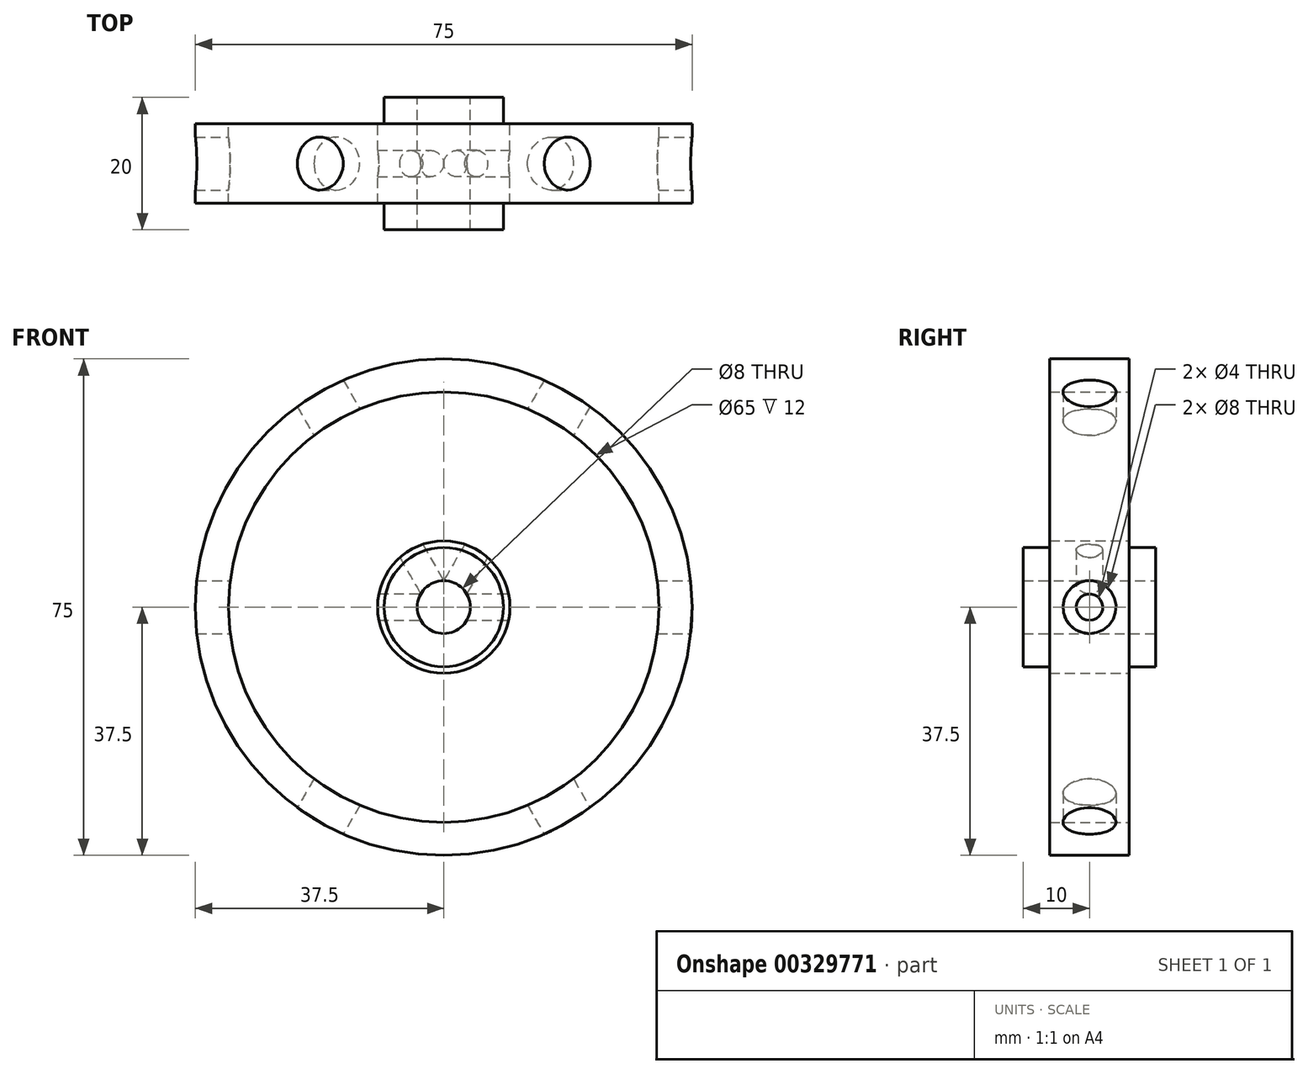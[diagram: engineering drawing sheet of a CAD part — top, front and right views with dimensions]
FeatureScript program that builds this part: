
annotation { "Feature Type Name" : "Feature", "Feature Type Description" : "" }
export const myFeature = defineFeature(function(context is Context, id is Id, definition is map)
    precondition{}
    {
        {
            var Q0;
            Q0=qCreatedBy(makeId("Front.planeOp"),FACE);
            var sketch = newSketch(context, id + "F0", { "sketchPlane" : qUnion([Q0])});
            skCircle(sketch, "E0", {"center": v(0, 0) * mm, "radius": 37.5 * mm});
            skCircle(sketch, "E1", {"center": v(0, 0) * mm, "radius": 32.5 * mm});
            skSolve(sketch);
        }
        {
            var Q0;
            Q0 = qSketchRegion(id + "F0", true);
            extrude(context, id + "F1", {"entities" : qUnion([Q0]), "depth" : 12 * mm, "symmetric" : true});
        }
        {
            var Q0;
            Q0=qCreatedBy(makeId("Right.planeOp"),FACE);
            cPlane(context, id + "F2", {"entities" : qUnion([Q0]), "cplaneType" : CPlaneType.OFFSET, "offset" : 37.5 * mm, "width" : 150 * mm, "height" : 150 * mm});
        }
        {
            var Q0;
            Q0=qCreatedBy(id+"F2.planeOp",FACE);
            var sketch = newSketch(context, id + "F3", { "sketchPlane" : qUnion([Q0])});
            skCircle(sketch, "E2", {"center": v(0, 0) * mm, "radius": 4 * mm});
            skSolve(sketch);
        }
        {
            var Q0;
            Q0 = qSketchRegion(id + "F3", true);
            extrude(context, id + "F4", {"entities" : qUnion([Q0]), "operationType" : NewBodyOperationType.REMOVE, "oppositeDirection" : true, "depth" : 115 * mm});
        }
        {
            var Q0;
            Q0=qCreatedBy(makeId("Right.planeOp"),FACE);
            var sketch = newSketch(context, id + "F5", { "sketchPlane" : qUnion([Q0])});
            skLineSegment(sketch, "E3", {"start": v(35.75, 0) * mm, "end": v(-32.2, 0) * mm, "construction": true});
            skSolve(sketch);
        }
        {
            var Q0;
            Q0=qCreatedBy(makeId("Top.planeOp"),FACE);
            var Q1;
            Q1 = qBodyType(qCreatedBy(id + "F5" ,EDGE), BodyType.WIRE);
            cPlane(context, id + "F6", {"entities" : qUnion([Q0, Q1]), "cplaneType" : CPlaneType.LINE_ANGLE, "offset" : 25 * mm, "angle" : 30 * degree, "width" : 150 * mm, "height" : 150 * mm});
        }
        {
            var Q0;
            Q0=qCreatedBy(id+"F6.planeOp",FACE);
            var sketch = newSketch(context, id + "F7", { "sketchPlane" : qUnion([Q0])});
            skCircle(sketch, "E4", {"center": v(0, 0) * mm, "radius": 4 * mm});
            skSolve(sketch);
        }
        {
            var Q0;
            Q0 = qSketchRegion(id + "F7", true);
            extrude(context, id + "F8", {"entities" : qUnion([Q0]), "operationType" : NewBodyOperationType.REMOVE, "oppositeDirection" : true, "depth" : 80 * mm, "symmetric" : true});
        }
        {
            var Q0;
            Q0=qCreatedBy(makeId("Top.planeOp"),FACE);
            var Q1;
            Q1 = qBodyType(qCreatedBy(id + "F5" ,EDGE), BodyType.WIRE);
            cPlane(context, id + "F9", {"entities" : qUnion([Q0, Q1]), "cplaneType" : CPlaneType.LINE_ANGLE, "offset" : 25 * mm, "angle" : 330 * degree, "width" : 150 * mm, "height" : 150 * mm});
        }
        {
            var Q0;
            Q0=qCreatedBy(id+"F9.planeOp",FACE);
            var sketch = newSketch(context, id + "F10", { "sketchPlane" : qUnion([Q0])});
            skCircle(sketch, "E5", {"center": v(0, 0) * mm, "radius": 4 * mm});
            skSolve(sketch);
        }
        {
            var Q0;
            Q0 = qSketchRegion(id + "F10", true);
            extrude(context, id + "F11", {"entities" : qUnion([Q0]), "operationType" : NewBodyOperationType.REMOVE, "oppositeDirection" : true, "depth" : 80 * mm, "symmetric" : true});
        }
        {
            var Q0;
            Q0=qCreatedBy(makeId("Front.planeOp"),FACE);
            var sketch = newSketch(context, id + "F12", { "sketchPlane" : qUnion([Q0])});
            skCircle(sketch, "E6", {"center": v(0, 0) * mm, "radius": 4 * mm});
            skCircle(sketch, "E7", {"center": v(0, 0) * mm, "radius": 10 * mm});
            skSolve(sketch);
        }
        {
            var Q0;
            Q0 = qSketchRegion(id + "F12", true);
            extrude(context, id + "F13", {"entities" : qUnion([Q0]), "depth" : 20 * mm, "symmetric" : true});
        }
        {
            var Q0;
            Q0=makeQuery(id+"F13.opExtrude","CAP_FACE",FACE,{"disambiguationData":[OSD([sQuery(id+"F12.wireOp",EDGE,"E6"),sQuery(id+"F12.wireOp",EDGE,"E7")])],"isStart":false});
            var sketch = newSketch(context, id + "F14", { "sketchPlane" : qUnion([Q0])});
            skCircle(sketch, "E8", {"center": v(0, 0) * mm, "radius": 9 * mm});
            skCircle(sketch, "E9", {"center": v(0, 0) * mm, "radius": 12.42 * mm});
            skSolve(sketch);
        }
        {
            var Q0;
            Q0 = qSketchRegion(id + "F14", true);
            extrude(context, id + "F15", {"entities" : qUnion([Q0]), "operationType" : NewBodyOperationType.REMOVE, "oppositeDirection" : true, "depth" : 4 * mm});
        }
        {
            var Q0;
            Q0=makeQuery(id+"F13.opExtrude","CAP_FACE",FACE,{"disambiguationData":[OSD([sQuery(id+"F12.wireOp",EDGE,"E6"),sQuery(id+"F12.wireOp",EDGE,"E7")])],"isStart":true});
            var sketch = newSketch(context, id + "F16", { "sketchPlane" : qUnion([Q0])});
            skCircle(sketch, "E10", {"center": v(0, 0) * mm, "radius": 9 * mm});
            skCircle(sketch, "E11", {"center": v(0, 0) * mm, "radius": 12.38 * mm});
            skSolve(sketch);
        }
        {
            var Q0;
            Q0 = qSketchRegion(id + "F16", true);
            extrude(context, id + "F17", {"entities" : qUnion([Q0]), "operationType" : NewBodyOperationType.REMOVE, "oppositeDirection" : true, "depth" : 4 * mm});
        }
        {
            var Q0;
            Q0=qCreatedBy(makeId("Right.planeOp"),FACE);
            var sketch = newSketch(context, id + "F18", { "sketchPlane" : qUnion([Q0])});
            skCircle(sketch, "E12", {"center": v(0, 0) * mm, "radius": 2 * mm});
            skSolve(sketch);
        }
        {
            var Q0;
            Q0 = qSketchRegion(id + "F18", true);
            extrude(context, id + "F19", {"entities" : qUnion([Q0]), "operationType" : NewBodyOperationType.REMOVE, "oppositeDirection" : true, "depth" : 25 * mm, "symmetric" : true});
        }
        {
            var Q0;
            Q0=qCreatedBy(id+"F6.planeOp",FACE);
            var sketch = newSketch(context, id + "F20", { "sketchPlane" : qUnion([Q0])});
            skCircle(sketch, "E13", {"center": v(0, 0) * mm, "radius": 2 * mm});
            skSolve(sketch);
        }
        {
            var Q0;
            Q0 = qSketchRegion(id + "F20", true);
            extrude(context, id + "F21", {"entities" : qUnion([Q0]), "operationType" : NewBodyOperationType.REMOVE, "oppositeDirection" : true, "depth" : 25 * mm});
        }
        {
            var Q0;
            Q0=qCreatedBy(id+"F9.planeOp",FACE);
            var sketch = newSketch(context, id + "F22", { "sketchPlane" : qUnion([Q0])});
            skCircle(sketch, "E14", {"center": v(0, 0) * mm, "radius": 2 * mm});
            skSolve(sketch);
        }
        {
            var Q0;
            Q0 = qSketchRegion(id + "F22", true);
            extrude(context, id + "F23", {"entities" : qUnion([Q0]), "operationType" : NewBodyOperationType.REMOVE, "oppositeDirection" : true, "depth" : 25 * mm});
        }
    });
